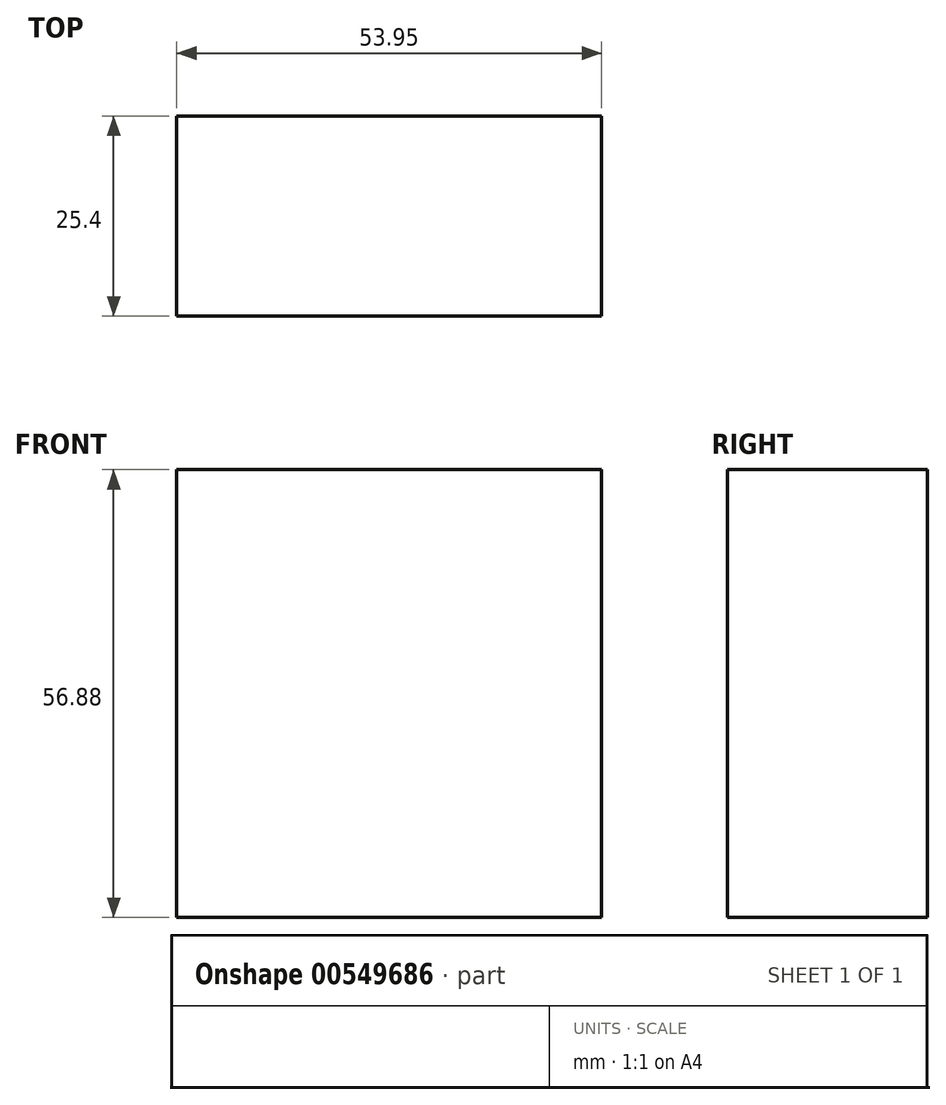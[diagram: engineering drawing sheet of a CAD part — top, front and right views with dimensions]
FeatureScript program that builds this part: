
annotation { "Feature Type Name" : "Feature", "Feature Type Description" : "" }
export const myFeature = defineFeature(function(context is Context, id is Id, definition is map)
    precondition{}
    {
        {
            var Q0;
            Q0=qCreatedBy(makeId("Front.planeOp"),FACE);
            var sketch = newSketch(context, id + "F0", { "sketchPlane" : qUnion([Q0])});
            skLineSegment(sketch, "E0.bottom", {"start": v(-53.95, 0) * mm, "end": v(0, 0) * mm});
            skLineSegment(sketch, "E0.top", {"start": v(-53.95, -56.88) * mm, "end": v(0, -56.88) * mm});
            skLineSegment(sketch, "E0.left", {"start": v(-53.95, 0) * mm, "end": v(-53.95, -56.88) * mm});
            skLineSegment(sketch, "E0.right", {"start": v(0, 0) * mm, "end": v(0, -56.88) * mm});
            skSolve(sketch);
        }
        {
            var Q0;
            Q0=makeQuery(id+"F0.imprint","IMPRINT",FACE,{"disambiguationData":[TD([[makeQuery(id+"F0.imprint","IMPRINT",EDGE,{"derivedFrom":sQuery(id+"F0.wireOp",EDGE,"E0.bottom")}),-1.0]])]});
            extrude(context, id + "F1", {"entities" : qUnion([Q0]), "depth" : 25.4 * mm, "offsetDistance" : 25.4 * mm});
        }
    });
